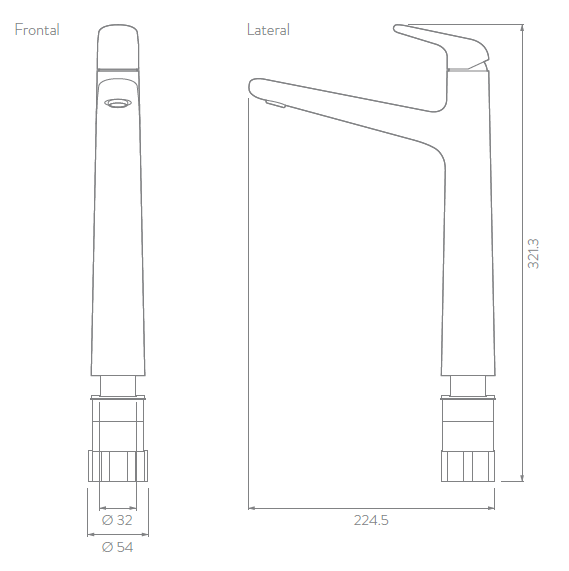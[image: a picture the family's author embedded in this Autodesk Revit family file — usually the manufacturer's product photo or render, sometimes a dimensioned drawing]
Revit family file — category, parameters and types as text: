
# Revit family: LQ1055551_Grifería Lavamanos Liquid Monocontrol Alta Mate Black
name_source: partatom
category: Plumbing Fixtures
units: mm (PartAtom-declared; Revit-internal decimal feet)

## family parameters
Always vertical = Yes
Cut with Voids When Loaded = No
OmniClass Number = 23.31.11.00
OmniClass Title = Faucets
Part Type = Normal
Room Calculation Point = No
Round Connector Dimension = Use Diameter
Shared = No
Work Plane-Based = No

## types (1)
- LQ1055551_Grifería Lavamanos Liquid Monocontrol Alta Mate Black
    Acabado = Corona_Mate_Black
    Alto = 321 mm  [stored 1.05315 ft]
    Altura de la grifería = Alta
    Ancho = 54 mm  [stored 0.177165 ft]
    Capacidad de flujo = 60 psi: 4,4 L/min
    Colección = Liquid
    Consumo de agua = 5.7 lt
    Creado por = IDD
    Description = La línea de griferías, duchas y accesorios Liquid se inspira en la tensión superficial del agua y en cómo esta crea formas armoniosas adaptándose al ambiente. Al igual que el agua, las superficies de las griferías Liquid juegan con la luz y los reflejos que fluyen alrededorde sus formas, sus líneas continuas y simplicidad formal proporcionan la ventaja práctica y limpieza sin esfuerzo.
Incluye la tecnología Ecostream, de ahorro de agua; y la tecnología ThermoControl, de control más preciso de la temperatura.
Incluye apertura con accionamiento central en frío que evita el encendido automático de calentadores y calderas ahorrando energía; además, es de fácil limpieza gracias al diseño que evita la acumulación de impurezas, es resistente a la corrosión, pelado y decoloración por agua y tiene recubrimientos no tóxicos.
    Fecha de creación = 09/10/2020
    Garantía = 30 años en estructura
    Garantías de otros componentes = 5 años en acabados
    Incluye = Cuerpo, Manija
    Linea = Liquid
    Longitud = 225 mm  [stored 0.738189 ft]
    Material = Metálico
    Peso  Bruto = 2.200 g. - 4,85 lb.
    Peso neto = 2.000 g. - 4,41 lb.
    Presión máxima recomendada = 125 psi (860 Kpa)
    Presión mínima recomendada = 20 psi (140 Kpa)
    Productos compatibles = Lavamanos tipo vessel
    Reference = LQ1055551
    Resistencia = Resistente a la corrosión pelado y decoloración por agua
    Sistema de accionamiento = Palanca monocontrol
    Tecnologías = DuraCrome EcoStream ThermoControl
    Temperaturas máxima de trabajo = 71°C / 159,8°F
    Temperaturas mínima de trabajo = 5°C / 41 °F
    Tipo de Chorro = Espumoso
    Tipo de Grifería = Monocontrol
    Tipo de manija/accionamiento = Palanca
    URL = https://corona.co
    Uso = Residencial
    Vida útil = 500.000 ciclos.

note: [stored X ft] marks values corroborated as IEEE doubles in the binary element streams (Revit-internal decimal feet)

## geometry (parser evidence)
native form markers: Sweep x10
no freeform markers — native parametric forms only
